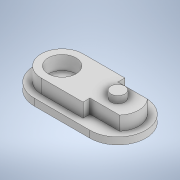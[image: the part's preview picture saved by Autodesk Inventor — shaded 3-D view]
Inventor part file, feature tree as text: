
AUTODESK INVENTOR PART (.ipt)
format: ipt  version: 2022.2 (Build 262287030, 287C)  size: 139,264 bytes
history: native  units: in
note: dims shown in document units (in); Inventor stores cm internally (conversion verified against a paired STEP export)
features: extrude x3, sketch x3
ambient origin geometry x8: Origin, YZ Plane, XZ Plane, XY Plane, X Axis, Y Axis, Z Axis, Center Point
bodies: Solid1 (feature_tree)
feature tree (6):
  extrude  "Extrusion1"  Depth=1.0in
  extrude  "Extrusion2"  Depth=0.75in
  extrude  "Extrusion3"  Depth=1.0in
  sketch  "Sketch1"  dims[d0=2.0in d1=1.0in]
  sketch  "Sketch2"  dims[d2=0.25in d3=0.0in d4=0.75in]
  sketch  "Sketch3"  dims[d5=1.5in d6=1.0in d7=1.0in d8=0.5in d9=0.0in d10=0.5in d11=0.25in d12=0.0in]
